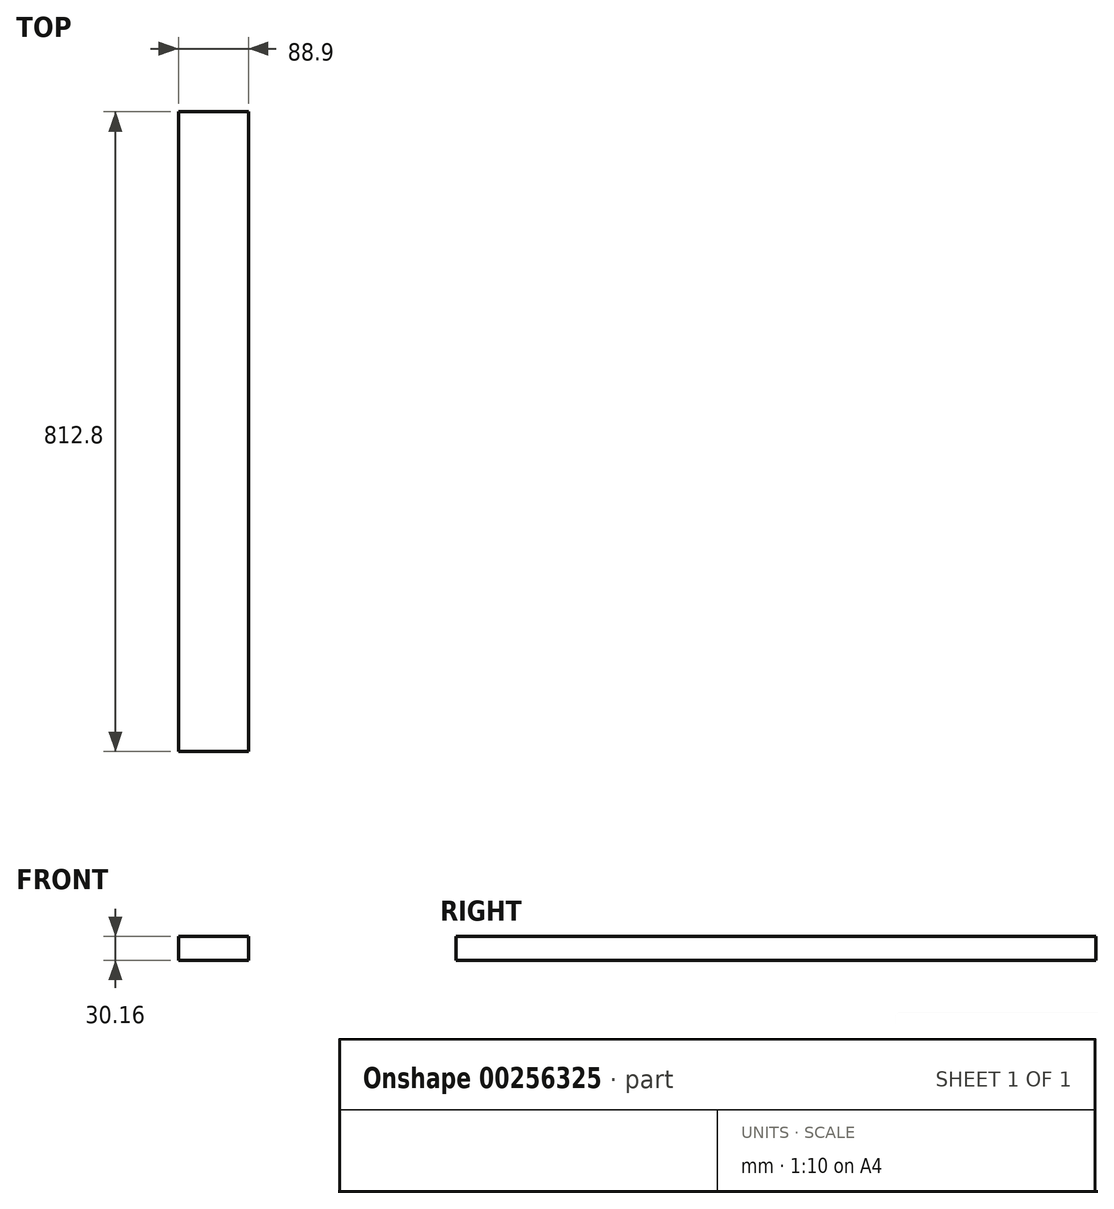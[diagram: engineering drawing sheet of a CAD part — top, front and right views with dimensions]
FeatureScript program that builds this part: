
annotation { "Feature Type Name" : "Feature", "Feature Type Description" : "" }
export const myFeature = defineFeature(function(context is Context, id is Id, definition is map)
    precondition{}
    {
        {
            var Q0;
            Q0=qCreatedBy(makeId("Front.planeOp"),FACE);
            var sketch = newSketch(context, id + "F0", { "sketchPlane" : qUnion([Q0])});
            skLineSegment(sketch, "E0.bottom", {"start": v(-44.45, 15.08) * mm, "end": v(44.45, 15.08) * mm});
            skLineSegment(sketch, "E0.top", {"start": v(-44.45, -15.08) * mm, "end": v(44.45, -15.08) * mm});
            skLineSegment(sketch, "E0.left", {"start": v(-44.45, 15.08) * mm, "end": v(-44.45, -15.08) * mm});
            skLineSegment(sketch, "E0.right", {"start": v(44.45, 15.08) * mm, "end": v(44.45, -15.08) * mm});
            skSolve(sketch);
        }
        {
            var Q0;
            Q0=qSketchRegion(id+"F0",true);
            extrude(context, id + "F1", {"entities" : qUnion([Q0]), "endBound" : BoundingType.SYMMETRIC, "depth" : 812.8 * mm});
        }
    });
